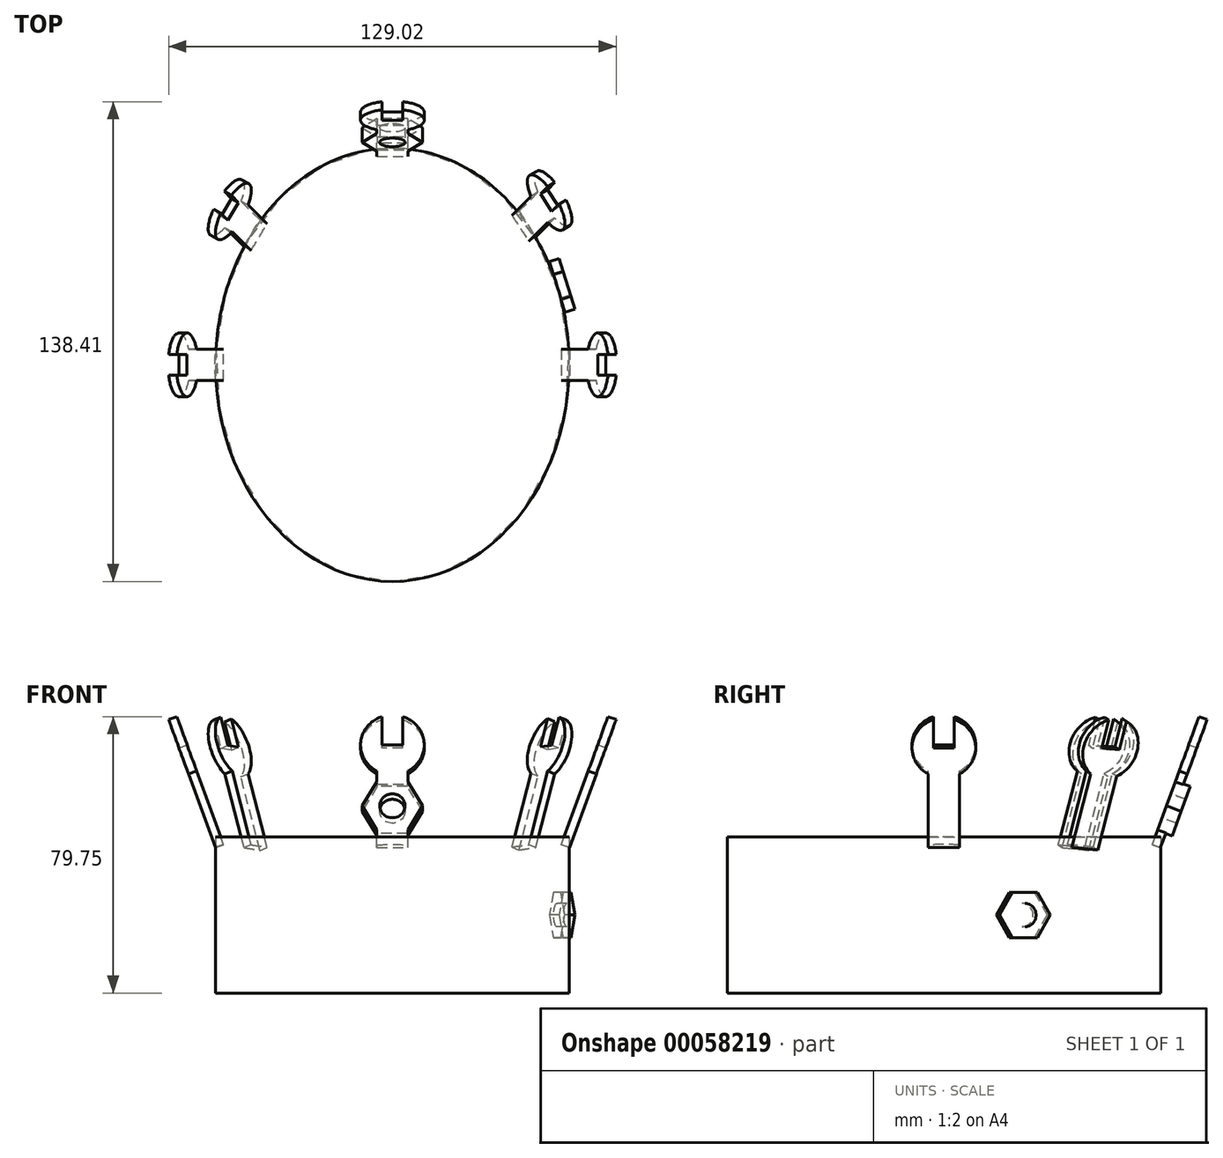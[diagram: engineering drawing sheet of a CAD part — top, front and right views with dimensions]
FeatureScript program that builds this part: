
annotation { "Feature Type Name" : "Feature", "Feature Type Description" : "" }
export const myFeature = defineFeature(function(context is Context, id is Id, definition is map)
    precondition{}
    {
        {
            var Q0;
            Q0=qCreatedBy(makeId("Top.planeOp"),FACE);
            var sketch = newSketch(context, id + "F0", { "sketchPlane" : qUnion([Q0])});
            skEllipse(sketch, "E0", {"center": v(0, 0) * mm, "majorRadius": 62.5 * mm, "minorRadius": 51 * mm, "majorAxis": v(0, -1)});
            skFitSpline(sketch, "E1.0", {"points": [v(-2.38, -59.95) * mm, v(0, -60.02) * mm, v(2.38, -59.95) * mm, v(5.53, -59.66) * mm, v(9.42, -58.95) * mm, v(13.98, -57.55) * mm, v(18.41, -55.6) * mm, v(22.68, -53.13) * mm, v(26.75, -50.15) * mm, v(29.95, -47.24) * mm, v(32.38, -44.68) * mm, v(34.14, -42.63) * mm, v(35.81, -40.48) * mm, v(37.91, -37.49) * mm, v(40.3, -33.53) * mm, v(42.77, -28.48) * mm, v(44.82, -23.15) * mm, v(46.44, -17.6) * mm, v(47.62, -11.87) * mm, v(48.22, -6.97) * mm, v(48.46, -3) * mm, v(48.52, 0) * mm, v(48.46, 3) * mm, v(48.22, 6.97) * mm, v(47.62, 11.87) * mm, v(46.44, 17.6) * mm, v(44.82, 23.15) * mm, v(42.77, 28.48) * mm, v(40.3, 33.53) * mm, v(37.91, 37.49) * mm, v(35.81, 40.48) * mm, v(34.14, 42.63) * mm, v(32.38, 44.68) * mm, v(29.95, 47.24) * mm, v(26.75, 50.15) * mm, v(22.68, 53.13) * mm, v(18.41, 55.6) * mm, v(13.98, 57.55) * mm, v(9.42, 58.95) * mm, v(5.53, 59.66) * mm, v(2.38, 59.95) * mm, v(0, 60.02) * mm, v(-2.38, 59.95) * mm, v(-5.53, 59.66) * mm, v(-9.42, 58.95) * mm, v(-13.98, 57.55) * mm, v(-18.41, 55.6) * mm, v(-22.68, 53.13) * mm, v(-26.75, 50.15) * mm, v(-29.95, 47.24) * mm, v(-32.38, 44.68) * mm, v(-34.14, 42.63) * mm, v(-35.81, 40.48) * mm, v(-37.91, 37.49) * mm, v(-40.3, 33.53) * mm, v(-42.77, 28.48) * mm, v(-44.82, 23.15) * mm, v(-46.44, 17.6) * mm, v(-47.62, 11.87) * mm, v(-48.22, 6.97) * mm, v(-48.46, 3) * mm, v(-48.52, 0) * mm, v(-48.46, -3) * mm, v(-48.22, -6.97) * mm, v(-47.62, -11.87) * mm, v(-46.44, -17.6) * mm, v(-44.82, -23.15) * mm, v(-42.77, -28.48) * mm, v(-40.3, -33.53) * mm, v(-37.91, -37.49) * mm, v(-35.81, -40.48) * mm, v(-34.14, -42.63) * mm, v(-32.38, -44.68) * mm, v(-29.95, -47.24) * mm, v(-26.75, -50.15) * mm, v(-22.68, -53.13) * mm, v(-18.41, -55.6) * mm, v(-13.98, -57.55) * mm, v(-9.42, -58.95) * mm, v(-5.53, -59.66) * mm, v(-2.38, -59.95) * mm, v(0, -60.02) * mm, v(2.38, -59.95) * mm, v(-2.38, -59.95) * mm]});
            skSolve(sketch);
        }
        {
            var Q0;
            Q0=makeQuery(id+"F0.imprint","IMPRINT",FACE,{"disambiguationData":[TD([[makeQuery(id+"F0.imprint","IMPRINT",EDGE,{"derivedFrom":sQuery(id+"F0.wireOp",EDGE,"E0")}),1.0]])]});
            extrude(context, id + "F1", {"entities" : qUnion([Q0]), "depth" : 45 * mm});
        }
        {
            var Q0;
            Q0=qCreatedBy(makeId("Right.planeOp"),FACE);
            cPlane(context, id + "F2", {"entities" : qUnion([Q0]), "cplaneType" : CPlaneType.OFFSET, "offset" : 51 * mm, "width" : 150 * mm, "height" : 150 * mm});
        }
        {
            var Q0;
            Q0=qCreatedBy(makeId("Front.planeOp"),FACE);
            var sketch = newSketch(context, id + "F3", { "sketchPlane" : qUnion([Q0])});
            skLineSegment(sketch, "E2.0", {"start": v(-51, 45) * mm, "end": v(51, 45) * mm});
            skLineSegment(sketch, "E3", {"start": v(49.75, 45) * mm, "end": v(63.43, 82.59) * mm});
            skSolve(sketch);
        }
        {
            var Q0;
            Q0=sQuery(id+"F3.wireOp",EDGE,"E3");
            cPlane(context, id + "F4", {"entities" : qUnion([Q0]), "cplaneType" : CPlaneType.LINE_ANGLE, "offset" : 150 * mm, "angle" : 0 * degree, "width" : 150 * mm, "height" : 150 * mm});
        }
        {
            var Q0;
            Q0=qCreatedBy(id+"F4.planeOp",FACE);
            var sketch = newSketch(context, id + "F5", { "sketchPlane" : qUnion([Q0])});
            skEllipse(sketch, "E4.0", {"center": v(0, 42.29) * mm, "majorRadius": 62.5 * mm, "minorRadius": 17.44 * mm, "majorAxis": v(-1, 0)});
            skLineSegment(sketch, "E5.bottom", {"start": v(-4.47, 59.68) * mm, "end": v(4.47, 59.68) * mm});
            skLineSegment(sketch, "E5.left", {"start": v(-4.47, 59.68) * mm, "end": v(-4.47, 82.34) * mm});
            skLineSegment(sketch, "E5.right", {"start": v(4.47, 59.68) * mm, "end": v(4.47, 82.34) * mm});
            skLineSegment(sketch, "E6.top", {"start": v(-3, 90.35) * mm, "end": v(3, 90.35) * mm});
            skLineSegment(sketch, "E6.left", {"start": v(-3, 99.02) * mm, "end": v(-3, 90.35) * mm});
            skLineSegment(sketch, "E6.right", {"start": v(3, 99.02) * mm, "end": v(3, 90.35) * mm});
            skArc(sketch, "E7", {"start": v(4.47, 82.34) * mm, "mid": v(9.14, 91.16) * mm, "end": v(3, 99.02) * mm});
            skArc(sketch, "E8.trimOffspring", {"start": v(-3, 99.02) * mm, "mid": v(-9.14, 91.16) * mm, "end": v(-4.47, 82.34) * mm});
            skSolve(sketch);
        }
        {
            var Q0;
            {var subQ1=sQuery(id+"F5.wireOp",EDGE,"E5.left");Q0=makeQuery(id+"F5.imprint","IMPRINT",FACE,{"disambiguationData":[TD([[makeQuery(id+"F5.imprint","IMPRINT",EDGE,{"derivedFrom":subQ1}),-1.0]])]});}
            extrude(context, id + "F6", {"entities" : qUnion([Q0]), "operationType" : NewBodyOperationType.ADD, "depth" : 1.25 * mm, "hasSecondDirection" : true, "secondDirectionOppositeDirection" : true, "secondDirectionDepth" : 1.25 * mm});
        }
        {
            var Q0;
            Q0=makeQuery(id+"F6.opExtrude","SWEPT_BODY",BODY,{"disambiguationData":[OSD([sQuery(id+"F5.wireOp",EDGE,"E4.0"),sQuery(id+"F5.wireOp",EDGE,"E5.left"),sQuery(id+"F5.wireOp",EDGE,"E5.right"),sQuery(id+"F5.wireOp",EDGE,"E6.top"),sQuery(id+"F5.wireOp",EDGE,"E6.left"),sQuery(id+"F5.wireOp",EDGE,"E6.right"),sQuery(id+"F5.wireOp",EDGE,"E7"),sQuery(id+"F5.wireOp",EDGE,"E8.trimOffspring")])]});
            transform(context, id + "F7", {"entities" : qUnion([Q0]), "transformType" : TransformType.TRANSLATION_3D, "dx" : 0 * mm, "dy" : 0 * mm, "dz" : -3 * mm, "makeCopy" : false});
        }
        {
            var Q0;
            Q0=makeQuery(id+"F1.opExtrude","CAP_FACE",FACE,{"disambiguationData":[OSD([sQuery(id+"F0.wireOp",EDGE,"E0"),sQuery(id+"F0.wireOp",EDGE,"E1.0")])],"isStart":false});
            var sketch = newSketch(context, id + "F8", { "sketchPlane" : qUnion([Q0])});
            skEllipse(sketch, "E9.0", {"center": v(0, 0) * mm, "majorRadius": 62.5 * mm, "minorRadius": 51 * mm, "majorAxis": v(0, -1)});
            skLineSegment(sketch, "E10", {"start": v(0, 0) * mm, "end": v(0, 62.5) * mm, "construction": true});
            skSolve(sketch);
        }
        {
            var Q0;
            Q0=qCreatedBy(makeId("Front.planeOp"),FACE);
            var sketch = newSketch(context, id + "F9", { "sketchPlane" : qUnion([Q0])});
            skLineSegment(sketch, "E11.0", {"start": v(-51, 45) * mm, "end": v(51, 45) * mm, "construction": true});
            skLineSegment(sketch, "E12", {"start": v(0, 45) * mm, "end": v(0, 95.05) * mm, "construction": true});
            skSolve(sketch);
        }
        {
            var Q0;
            Q0=makeQuery(id+"F6.opExtrude","SWEPT_BODY",BODY,{"disambiguationData":[OSD([sQuery(id+"F5.wireOp",EDGE,"E4.0"),sQuery(id+"F5.wireOp",EDGE,"E5.left"),sQuery(id+"F5.wireOp",EDGE,"E5.right"),sQuery(id+"F5.wireOp",EDGE,"E6.top"),sQuery(id+"F5.wireOp",EDGE,"E6.left"),sQuery(id+"F5.wireOp",EDGE,"E6.right"),sQuery(id+"F5.wireOp",EDGE,"E7"),sQuery(id+"F5.wireOp",EDGE,"E8.trimOffspring")])]});
            var Q1;
            Q1=sQuery(id+"F9.wireOp",EDGE,"E12");
            circularPattern(context, id + "F10", {"entities" : qUnion([Q0]), "axis" : qUnion([Q1]), "angle" : 45 * degree, "instanceCount" : 5});
        }
        {
            var Q0;
            Q0=makeQuery(id+"F10.opPattern","COPY",BODY,{"derivedFrom":makeQuery(id+"F6.opExtrude","SWEPT_BODY",BODY,{"disambiguationData":[OSD([sQuery(id+"F5.wireOp",EDGE,"E4.0"),sQuery(id+"F5.wireOp",EDGE,"E5.left"),sQuery(id+"F5.wireOp",EDGE,"E5.right"),sQuery(id+"F5.wireOp",EDGE,"E6.top"),sQuery(id+"F5.wireOp",EDGE,"E6.left"),sQuery(id+"F5.wireOp",EDGE,"E6.right"),sQuery(id+"F5.wireOp",EDGE,"E7"),sQuery(id+"F5.wireOp",EDGE,"E8.trimOffspring")])]}),"instanceName":"2"});
            transform(context, id + "F11", {"entities" : qUnion([Q0]), "transformType" : TransformType.TRANSLATION_3D, "dx" : 0 * mm, "dy" : 11.4 * mm, "dz" : 0 * mm, "makeCopy" : false});
        }
        {
            var Q0;
            Q0=makeQuery(id+"F10.opPattern","COPY",BODY,{"derivedFrom":makeQuery(id+"F6.opExtrude","SWEPT_BODY",BODY,{"disambiguationData":[OSD([sQuery(id+"F5.wireOp",EDGE,"E4.0"),sQuery(id+"F5.wireOp",EDGE,"E5.left"),sQuery(id+"F5.wireOp",EDGE,"E5.right"),sQuery(id+"F5.wireOp",EDGE,"E6.top"),sQuery(id+"F5.wireOp",EDGE,"E6.left"),sQuery(id+"F5.wireOp",EDGE,"E6.right"),sQuery(id+"F5.wireOp",EDGE,"E7"),sQuery(id+"F5.wireOp",EDGE,"E8.trimOffspring")])]}),"instanceName":"3"});
            var Q1;
            Q1=makeQuery(id+"F10.opPattern","COPY",EDGE,{"derivedFrom":makeQuery(id+"F6.opExtrude","CAP_EDGE",EDGE,{"disambiguationData":[OSD([sQuery(id+"F5.wireOp",EDGE,"E5.right")])],"isStart":false}),"instanceName":"3"});
            transform(context, id + "F12", {"entities" : qUnion([Q0]), "transformType" : TransformType.ROTATION, "transformAxis" : qUnion([Q1]), "angle" : 15 * degree, "makeCopy" : false});
        }
        {
            var Q0;
            Q0=makeQuery(id+"F10.opPattern","COPY",BODY,{"derivedFrom":makeQuery(id+"F6.opExtrude","SWEPT_BODY",BODY,{"disambiguationData":[OSD([sQuery(id+"F5.wireOp",EDGE,"E4.0"),sQuery(id+"F5.wireOp",EDGE,"E5.left"),sQuery(id+"F5.wireOp",EDGE,"E5.right"),sQuery(id+"F5.wireOp",EDGE,"E6.top"),sQuery(id+"F5.wireOp",EDGE,"E6.left"),sQuery(id+"F5.wireOp",EDGE,"E6.right"),sQuery(id+"F5.wireOp",EDGE,"E7"),sQuery(id+"F5.wireOp",EDGE,"E8.trimOffspring")])]}),"instanceName":"3"});
            transform(context, id + "F13", {"entities" : qUnion([Q0]), "transformType" : TransformType.TRANSLATION_3D, "dx" : -3.53 * mm, "dy" : 1.2 * mm, "dz" : 0 * mm, "makeCopy" : false});
        }
        {
            var Q0;
            Q0=makeQuery(id+"F10.opPattern","COPY",BODY,{"derivedFrom":makeQuery(id+"F6.opExtrude","SWEPT_BODY",BODY,{"disambiguationData":[OSD([sQuery(id+"F5.wireOp",EDGE,"E4.0"),sQuery(id+"F5.wireOp",EDGE,"E5.left"),sQuery(id+"F5.wireOp",EDGE,"E5.right"),sQuery(id+"F5.wireOp",EDGE,"E6.top"),sQuery(id+"F5.wireOp",EDGE,"E6.left"),sQuery(id+"F5.wireOp",EDGE,"E6.right"),sQuery(id+"F5.wireOp",EDGE,"E7"),sQuery(id+"F5.wireOp",EDGE,"E8.trimOffspring")])]}),"instanceName":"1"});
            var Q1;
            Q1=makeQuery(id+"F10.opPattern","COPY",EDGE,{"derivedFrom":makeQuery(id+"F6.opExtrude","CAP_EDGE",EDGE,{"disambiguationData":[OSD([sQuery(id+"F5.wireOp",EDGE,"E5.left")])],"isStart":true}),"instanceName":"1"});
            transform(context, id + "F14", {"entities" : qUnion([Q0]), "transformType" : TransformType.ROTATION, "transformAxis" : qUnion([Q1]), "angle" : 13 * degree, "oppositeDirection" : true, "makeCopy" : false});
        }
        {
            var Q0;
            Q0=makeQuery(id+"F10.opPattern","COPY",BODY,{"derivedFrom":makeQuery(id+"F6.opExtrude","SWEPT_BODY",BODY,{"disambiguationData":[OSD([sQuery(id+"F5.wireOp",EDGE,"E4.0"),sQuery(id+"F5.wireOp",EDGE,"E5.left"),sQuery(id+"F5.wireOp",EDGE,"E5.right"),sQuery(id+"F5.wireOp",EDGE,"E6.top"),sQuery(id+"F5.wireOp",EDGE,"E6.left"),sQuery(id+"F5.wireOp",EDGE,"E6.right"),sQuery(id+"F5.wireOp",EDGE,"E7"),sQuery(id+"F5.wireOp",EDGE,"E8.trimOffspring")])]}),"instanceName":"1"});
            transform(context, id + "F15", {"entities" : qUnion([Q0]), "transformType" : TransformType.TRANSLATION_3D, "dx" : 1.71 * mm, "dy" : 4.35 * mm, "dz" : 0 * mm, "makeCopy" : false});
        }
        {
            var Q0;
            Q0=makeQuery(id+"F10.opPattern","COPY",FACE,{"derivedFrom":makeQuery(id+"F6.opExtrude","CAP_FACE",FACE,{"disambiguationData":[OSD([sQuery(id+"F5.wireOp",EDGE,"E4.0"),sQuery(id+"F5.wireOp",EDGE,"E5.left"),sQuery(id+"F5.wireOp",EDGE,"E5.right"),sQuery(id+"F5.wireOp",EDGE,"E6.top"),sQuery(id+"F5.wireOp",EDGE,"E6.left"),sQuery(id+"F5.wireOp",EDGE,"E6.right"),sQuery(id+"F5.wireOp",EDGE,"E7"),sQuery(id+"F5.wireOp",EDGE,"E8.trimOffspring")])],"isStart":false}),"instanceName":"2"});
            var sketch = newSketch(context, id + "F16", { "sketchPlane" : qUnion([Q0])});
            skLineSegment(sketch, "E13", {"start": v(0, 91.43) * mm, "end": v(0, 70) * mm, "construction": true});
            skCircle(sketch, "E14.cCircle", {"center": v(0, 72.7) * mm, "radius": 7.58 * mm, "construction": true});
            skLineSegment(sketch, "E14.0", {"start": v(4.38, 65.12) * mm, "end": v(-4.38, 65.12) * mm});
            skLineSegment(sketch, "E14.1", {"start": v(-4.38, 65.12) * mm, "end": v(-8.75, 72.7) * mm});
            skLineSegment(sketch, "E14.2", {"start": v(-8.75, 72.7) * mm, "end": v(-4.38, 80.28) * mm});
            skLineSegment(sketch, "E14.3", {"start": v(-4.38, 80.28) * mm, "end": v(4.38, 80.28) * mm});
            skLineSegment(sketch, "E14.4", {"start": v(4.38, 80.28) * mm, "end": v(8.75, 72.7) * mm});
            skLineSegment(sketch, "E14.5", {"start": v(8.75, 72.7) * mm, "end": v(4.38, 65.12) * mm});
            skPoint(sketch, "E14.0.midPoint", {"position": v(0, 65.12) * mm});
            skCircle(sketch, "E15", {"center": v(0, 72.7) * mm, "radius": 3.67 * mm});
            skSolve(sketch);
        }
        {
            var Q0;
            {var subQ5=sQuery(id+"F16.wireOp",EDGE,"E14.0");Q0=makeQuery(id+"F16.imprint","IMPRINT",FACE,{"disambiguationData":[TD([[makeQuery(id+"F16.imprint","IMPRINT",EDGE,{"derivedFrom":subQ5}),-1.0]])]});}
            var Q1;
            {var subQ0=sQuery(id+"F16.wireOp",EDGE,"E14.2");var subQ1=sQuery(id+"F16.wireOp",EDGE,"E14.1");var subQ2=makeQuery(id+"F16.imprint","INTERSECT",VERTEX,{"derivedFrom":[subQ1,subQ0]});Q1=makeQuery(id+"F16.imprint","IMPRINT",FACE,{"disambiguationData":[TD([[makeQuery(id+"F16.imprint","IMPRINT",EDGE,{"disambiguationData":[TD([[subQ2,1.0]])],"derivedFrom":subQ1}),-1.0]])]});}
            var Q2;
            {var subQ0=sQuery(id+"F16.wireOp",EDGE,"E14.5");var subQ1=sQuery(id+"F16.wireOp",EDGE,"E14.4");var subQ2=makeQuery(id+"F16.imprint","INTERSECT",VERTEX,{"derivedFrom":[subQ1,subQ0]});Q2=makeQuery(id+"F16.imprint","IMPRINT",FACE,{"disambiguationData":[TD([[makeQuery(id+"F16.imprint","IMPRINT",EDGE,{"disambiguationData":[TD([[subQ2,1.0]])],"derivedFrom":subQ1}),-1.0]])]});}
            extrude(context, id + "F17", {"entities" : qUnion([Q0, Q1, Q2]), "operationType" : NewBodyOperationType.ADD, "depth" : 2 * mm, "hasSecondDirection" : true, "secondDirectionOppositeDirection" : true, "secondDirectionDepth" : 2.5 * mm});
        }
        {
            var Q0;
            Q0=makeQuery(id+"F17.boolean.opBoolean","SPLIT",FACE,{"disambiguationData":[TD([makeQuery(id+"F17.opExtrude","SWEPT_FACE",FACE,{"disambiguationData":[OSD([sQuery(id+"F16.wireOp",EDGE,"E15")])]})])],"derivedFrom":makeQuery(id+"F10.opPattern","COPY",FACE,{"derivedFrom":makeQuery(id+"F6.opExtrude","CAP_FACE",FACE,{"disambiguationData":[OSD([sQuery(id+"F5.wireOp",EDGE,"E4.0"),sQuery(id+"F5.wireOp",EDGE,"E5.left"),sQuery(id+"F5.wireOp",EDGE,"E5.right"),sQuery(id+"F5.wireOp",EDGE,"E6.top"),sQuery(id+"F5.wireOp",EDGE,"E6.left"),sQuery(id+"F5.wireOp",EDGE,"E6.right"),sQuery(id+"F5.wireOp",EDGE,"E7"),sQuery(id+"F5.wireOp",EDGE,"E8.trimOffspring")])],"isStart":false}),"instanceName":"2"})});
            extrude(context, id + "F18", {"entities" : qUnion([Q0]), "operationType" : NewBodyOperationType.REMOVE, "endBound" : BoundingType.THROUGH_ALL, "oppositeDirection" : true, "depth" : 25 * mm});
        }
        {
            var Q0;
            Q0=qCreatedBy(id+"F2.planeOp",FACE);
            var sketch = newSketch(context, id + "F19", { "sketchPlane" : qUnion([Q0])});
            skLineSegment(sketch, "E16.0", {"start": v(62.5, 45) * mm, "end": v(-62.5, 45) * mm, "construction": true});
            skLineSegment(sketch, "E17.0", {"start": v(62.5, 0) * mm, "end": v(-62.5, 0) * mm, "construction": true});
            skLineSegment(sketch, "E18", {"start": v(23.39, 45) * mm, "end": v(23.39, 0) * mm, "construction": true});
            skLineSegment(sketch, "E19", {"start": v(23.39, 22.5) * mm, "end": v(5.44, 22.5) * mm, "construction": true});
            skCircle(sketch, "E20.cCircle", {"center": v(23.39, 22.5) * mm, "radius": 6.58 * mm, "construction": true});
            skLineSegment(sketch, "E20.0", {"start": v(27.19, 15.92) * mm, "end": v(19.59, 15.92) * mm});
            skLineSegment(sketch, "E20.1", {"start": v(19.59, 15.92) * mm, "end": v(15.79, 22.5) * mm});
            skLineSegment(sketch, "E20.2", {"start": v(15.79, 22.5) * mm, "end": v(19.59, 29.08) * mm});
            skLineSegment(sketch, "E20.3", {"start": v(19.59, 29.08) * mm, "end": v(27.19, 29.08) * mm});
            skLineSegment(sketch, "E20.4", {"start": v(27.19, 29.08) * mm, "end": v(30.99, 22.5) * mm});
            skLineSegment(sketch, "E20.5", {"start": v(30.99, 22.5) * mm, "end": v(27.19, 15.92) * mm});
            skPoint(sketch, "E20.0.midPoint", {"position": v(23.39, 15.92) * mm});
            skCircle(sketch, "E21", {"center": v(23.39, 22.5) * mm, "radius": 3.38 * mm});
            skSolve(sketch);
        }
        {
            var Q0;
            Q0=makeQuery(id+"F19.imprint","IMPRINT",FACE,{"disambiguationData":[TD([[makeQuery(id+"F19.imprint","IMPRINT",EDGE,{"derivedFrom":sQuery(id+"F19.wireOp",EDGE,"E20.0")}),-1.0]])]});
            extrude(context, id + "F20", {"entities" : qUnion([Q0]), "depth" : 3 * mm});
        }
        {
            var Q0;
            Q0=makeQuery(id+"F20.opExtrude","CAP_FACE",FACE,{"disambiguationData":[OSD([sQuery(id+"F19.wireOp",EDGE,"E20.0"),sQuery(id+"F19.wireOp",EDGE,"E20.1"),sQuery(id+"F19.wireOp",EDGE,"E20.2"),sQuery(id+"F19.wireOp",EDGE,"E20.3"),sQuery(id+"F19.wireOp",EDGE,"E20.4"),sQuery(id+"F19.wireOp",EDGE,"E20.5"),sQuery(id+"F19.wireOp",EDGE,"E21")])],"isStart":true});
            var sketch = newSketch(context, id + "F21", { "sketchPlane" : qUnion([Q0])});
            skLineSegment(sketch, "E22", {"start": v(-19.59, 29.08) * mm, "end": v(-19.59, 15.92) * mm, "construction": true});
            skSolve(sketch);
        }
        {
            var Q0;
            Q0=makeQuery(id+"F20.opExtrude","SWEPT_BODY",BODY,{"disambiguationData":[OSD([sQuery(id+"F19.wireOp",EDGE,"E20.0"),sQuery(id+"F19.wireOp",EDGE,"E20.1"),sQuery(id+"F19.wireOp",EDGE,"E20.2"),sQuery(id+"F19.wireOp",EDGE,"E20.3"),sQuery(id+"F19.wireOp",EDGE,"E20.4"),sQuery(id+"F19.wireOp",EDGE,"E20.5"),sQuery(id+"F19.wireOp",EDGE,"E21")])]});
            var Q1;
            Q1=sQuery(id+"F21.wireOp",EDGE,"E22");
            transform(context, id + "F22", {"entities" : qUnion([Q0]), "transformType" : TransformType.ROTATION, "transformAxis" : qUnion([Q1]), "angle" : 17.17 * degree, "oppositeDirection" : true, "makeCopy" : false});
        }
        {
            var Q0;
            Q0=makeQuery(id+"F20.opExtrude","SWEPT_BODY",BODY,{"disambiguationData":[OSD([sQuery(id+"F19.wireOp",EDGE,"E20.0"),sQuery(id+"F19.wireOp",EDGE,"E20.1"),sQuery(id+"F19.wireOp",EDGE,"E20.2"),sQuery(id+"F19.wireOp",EDGE,"E20.3"),sQuery(id+"F19.wireOp",EDGE,"E20.4"),sQuery(id+"F19.wireOp",EDGE,"E20.5"),sQuery(id+"F19.wireOp",EDGE,"E21")])]});
            transform(context, id + "F23", {"entities" : qUnion([Q0]), "transformType" : TransformType.TRANSLATION_3D, "dx" : -2.4 * mm, "dy" : -0.73 * mm, "dz" : 0 * mm, "makeCopy" : false});
        }
    });
